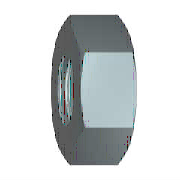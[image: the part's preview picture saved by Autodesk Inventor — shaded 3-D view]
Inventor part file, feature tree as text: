
AUTODESK INVENTOR PART (.ipt)
format: ipt  version: 2023 (Build 270158000, 158)  size: 172,032 bytes
history: native  units: mm (DEFAULTED — no unit token found)
features: sketch x3, other x2, extrude x1, hole x1, plane x1
ambient origin geometry x7: Origin, YZ Plane, XZ Plane, X Axis, Y Axis, Z Axis, Center Point
bodies: Solid1 (feature_tree)
feature tree (8):
  extrude  "Corpo"  Depth=31.176915mm
  other  "Smusso1"
  hole  "Filettatura"  [1 undecoded]
  other  "Work Axis1"
  plane  "Work Plane1"
  sketch  "Schizzo1"
  sketch  "Schizzo2"
  sketch  "Schizzo3"
note: 1 required parameter value undecoded (feature->parameter linkage not recoverable at this tier; creation-order binding heuristic only, values carry confidence <= 0.55)
